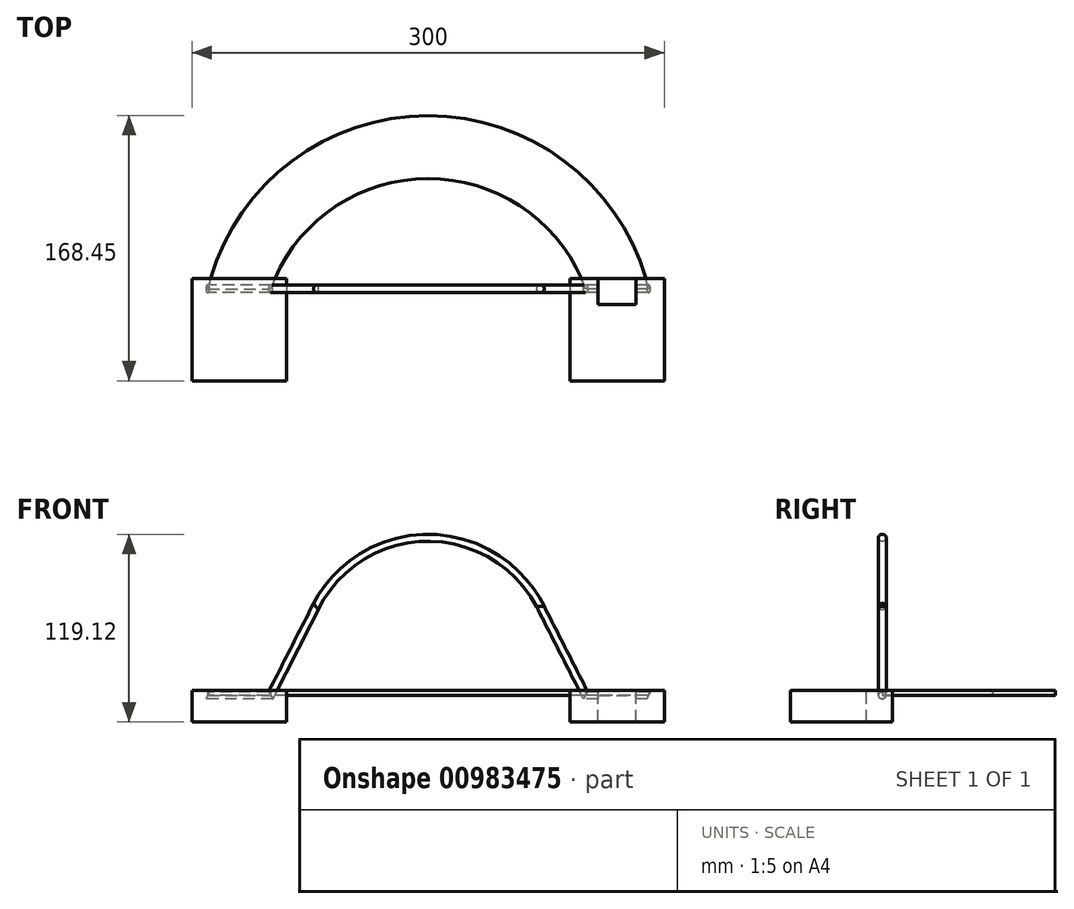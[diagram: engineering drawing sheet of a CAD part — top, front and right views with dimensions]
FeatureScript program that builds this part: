
annotation { "Feature Type Name" : "Feature", "Feature Type Description" : "" }
export const myFeature = defineFeature(function(context is Context, id is Id, definition is map)
    precondition{}
    {
        {
            var Q0;
            Q0=qCreatedBy(makeId("Top.planeOp"),FACE);
            var sketch = newSketch(context, id + "F0", { "sketchPlane" : qUnion([Q0])});
            skLineSegment(sketch, "E0", {"start": v(-140, 0) * mm, "end": v(140, 0) * mm});
            skPoint(sketch, "E1", {"position": v(0, 0) * mm});
            skCircle(sketch, "E2", {"center": v(0, 0) * mm, "radius": 97.97 * mm});
            skSolve(sketch);
        }
        {
            var Q0;
            Q0=qCreatedBy(makeId("Top.planeOp"),FACE);
            var sketch = newSketch(context, id + "F1", { "sketchPlane" : qUnion([Q0])});
            skLineSegment(sketch, "E3", {"start": v(-100, 0) * mm, "end": v(100, 0) * mm});
            skPoint(sketch, "E4", {"position": v(0, 0) * mm});
            skLineSegment(sketch, "E5", {"start": v(0, 0) * mm, "end": v(0, 70) * mm});
            skArc(sketch, "E6", {"start": v(100, 0) * mm, "mid": v(0, 70) * mm, "end": v(-100, 0) * mm});
            skSolve(sketch);
        }
        {
            var Q0;
            Q0=qCreatedBy(makeId("Top.planeOp"),FACE);
            var sketch = newSketch(context, id + "F2", { "sketchPlane" : qUnion([Q0])});
            skPoint(sketch, "E7", {"position": v(0, 0) * mm});
            skLineSegment(sketch, "E8", {"start": v(0, 0) * mm, "end": v(0, 70) * mm});
            skArc(sketch, "E9", {"start": v(100, 0) * mm, "mid": v(0, 70) * mm, "end": v(-100, 0) * mm});
            skArc(sketch, "E10.0", {"start": v(121.07, 0) * mm, "mid": v(0, 90) * mm, "end": v(-121.07, 0) * mm});
            skLineSegment(sketch, "E11", {"start": v(-140, 0) * mm, "end": v(-100, 0) * mm});
            skLineSegment(sketch, "E12", {"start": v(0, 0) * mm, "end": v(0, 110) * mm});
            skLineSegment(sketch, "E13", {"start": v(140, 0) * mm, "end": v(100, 0) * mm});
            skArc(sketch, "E14", {"start": v(140, 0) * mm, "mid": v(0, 110) * mm, "end": v(-140, 0) * mm});
            skLineSegment(sketch, "E15.trimOffspring", {"start": v(100, 0) * mm, "end": v(140, 0) * mm});
            skLineSegment(sketch, "E16.trimOffspring", {"start": v(-100, 0) * mm, "end": v(-140, 0) * mm});
            skSolve(sketch);
        }
        {
            var Q0;
            Q0=qCreatedBy(makeId("Front.planeOp"),FACE);
            var sketch = newSketch(context, id + "F3", { "sketchPlane" : qUnion([Q0])});
            skLineSegment(sketch, "E17", {"start": v(0, 0) * mm, "end": v(0, 20) * mm});
            skPoint(sketch, "E18.0", {"position": v(100, 0) * mm});
            skPoint(sketch, "E19.0", {"position": v(-100, 0) * mm});
            skArc(sketch, "E20", {"start": v(71.27, 56.34) * mm, "mid": v(0, 100) * mm, "end": v(-71.27, 56.34) * mm});
            skLineSegment(sketch, "E21", {"start": v(-100, 0) * mm, "end": v(-71.27, 56.34) * mm});
            skLineSegment(sketch, "E22", {"start": v(100, 0) * mm, "end": v(71.27, 56.34) * mm});
            skSolve(sketch);
        }
        {
            var Q0;
            Q0=qCreatedBy(makeId("Top.planeOp"),FACE);
            var sketch = newSketch(context, id + "F4", { "sketchPlane" : qUnion([Q0])});
            skPoint(sketch, "E23.0", {"position": v(100, 0) * mm});
            skCircle(sketch, "E24", {"center": v(100, 0) * mm, "radius": 2.5 * mm});
            skSolve(sketch);
        }
        {
            var Q0;
            Q0=makeQuery(id+"F4.imprint","IMPRINT",FACE,{"disambiguationData":[TD([[makeQuery(id+"F4.imprint","IMPRINT",EDGE,{"derivedFrom":sQuery(id+"F4.wireOp",EDGE,"E24")}),1.0]])]});
            var Q1;
            Q1=sQuery(id+"F3.wireOp",EDGE,"E22");
            var Q2;
            Q2=sQuery(id+"F3.wireOp",EDGE,"E20");
            var Q3;
            Q3=sQuery(id+"F3.wireOp",EDGE,"E21");
            var Q4;
            Q4=sQuery(id+"F2.wireOp",EDGE,"E11");
            var Q5;
            Q5=sQuery(id+"F2.wireOp",EDGE,"E13");
            sweep(context, id + "F5", {"profiles" : qUnion([Q0]), "path" : qUnion([Q1, Q2, Q3, Q4, Q5])});
        }
        {
            var Q0;
            {var subQ0=sQuery(id+"F2.wireOp",EDGE,"E15.trimOffspring");var subQ1=sQuery(id+"F2.wireOp",EDGE,"E9");var subQ2=makeQuery(id+"F2.imprint","INTERSECT",VERTEX,{"derivedFrom":[subQ1,subQ0]});Q0=makeQuery(id+"F2.imprint","IMPRINT",FACE,{"disambiguationData":[TD([[makeQuery(id+"F2.imprint","IMPRINT",EDGE,{"disambiguationData":[TD([[subQ2,-1.0]])],"derivedFrom":subQ1}),-1.0]])]});}
            var Q1;
            {var subQ0=sQuery(id+"F2.wireOp",EDGE,"E16.trimOffspring");var subQ1=sQuery(id+"F2.wireOp",EDGE,"E9");var subQ2=makeQuery(id+"F2.imprint","INTERSECT",VERTEX,{"derivedFrom":[subQ1,subQ0]});Q1=makeQuery(id+"F2.imprint","IMPRINT",FACE,{"disambiguationData":[TD([[makeQuery(id+"F2.imprint","IMPRINT",EDGE,{"disambiguationData":[TD([[subQ2,1.0]])],"derivedFrom":subQ1}),-1.0]])]});}
            var Q2;
            {var subQ0=sQuery(id+"F2.wireOp",EDGE,"E16.trimOffspring");var subQ1=sQuery(id+"F2.wireOp",EDGE,"E10.0");var subQ2=makeQuery(id+"F2.imprint","INTERSECT",VERTEX,{"derivedFrom":[subQ1,subQ0]});Q2=makeQuery(id+"F2.imprint","IMPRINT",FACE,{"disambiguationData":[TD([[makeQuery(id+"F2.imprint","IMPRINT",EDGE,{"disambiguationData":[TD([[subQ2,1.0]])],"derivedFrom":subQ1}),-1.0]])]});}
            var Q3;
            {var subQ0=sQuery(id+"F2.wireOp",EDGE,"E15.trimOffspring");var subQ1=sQuery(id+"F2.wireOp",EDGE,"E10.0");var subQ2=makeQuery(id+"F2.imprint","INTERSECT",VERTEX,{"derivedFrom":[subQ1,subQ0]});Q3=makeQuery(id+"F2.imprint","IMPRINT",FACE,{"disambiguationData":[TD([[makeQuery(id+"F2.imprint","IMPRINT",EDGE,{"disambiguationData":[TD([[subQ2,-1.0]])],"derivedFrom":subQ1}),-1.0]])]});}
            extrude(context, id + "F6", {"entities" : qUnion([Q0, Q1, Q2, Q3]), "depth" : 3 * mm, "offsetDistance" : 25 * mm});
        }
        {
            var Q0;
            Q0=qCreatedBy(makeId("Right.planeOp"),FACE);
            cPlane(context, id + "F7", {"entities" : qUnion([Q0]), "cplaneType" : CPlaneType.OFFSET, "offset" : 150 * mm, "width" : 150 * mm, "height" : 150 * mm});
        }
        {
            var Q0;
            Q0=qCreatedBy(id+"F7.planeOp",FACE);
            var sketch = newSketch(context, id + "F8", { "sketchPlane" : qUnion([Q0])});
            skLineSegment(sketch, "E25.bottom", {"start": v(6.55, 3.11) * mm, "end": v(-58.45, 3.11) * mm});
            skLineSegment(sketch, "E25.top", {"start": v(6.55, -16.89) * mm, "end": v(-58.45, -16.89) * mm});
            skLineSegment(sketch, "E25.left", {"start": v(6.55, 3.11) * mm, "end": v(6.55, -16.89) * mm});
            skLineSegment(sketch, "E25.right", {"start": v(-58.45, 3.11) * mm, "end": v(-58.45, -16.89) * mm});
            skSolve(sketch);
        }
        {
            var Q0;
            Q0=makeQuery(id+"F8.imprint","IMPRINT",FACE,{"disambiguationData":[TD([[makeQuery(id+"F8.imprint","IMPRINT",EDGE,{"derivedFrom":sQuery(id+"F8.wireOp",EDGE,"E25.bottom")}),1.0]])]});
            extrude(context, id + "F9", {"entities" : qUnion([Q0]), "oppositeDirection" : true, "depth" : 60 * mm, "offsetDistance" : 25 * mm});
        }
        {
            var Q0;
            Q0=makeQuery(id+"F9.opExtrude","SWEPT_BODY",BODY,{"disambiguationData":[OSD([sQuery(id+"F8.wireOp",EDGE,"E25.bottom"),sQuery(id+"F8.wireOp",EDGE,"E25.top"),sQuery(id+"F8.wireOp",EDGE,"E25.left"),sQuery(id+"F8.wireOp",EDGE,"E25.right")])]});
            var Q1;
            Q1=qCreatedBy(makeId("Right.planeOp"),FACE);
            mirror(context, id + "F10", {"entities" : qUnion([Q0]), "mirrorPlane" : qUnion([Q1])});
        }
        {
            var Q0;
            Q0=makeQuery(id+"F9.opExtrude","SWEPT_FACE",FACE,{"disambiguationData":[OSD([sQuery(id+"F8.wireOp",EDGE,"E25.bottom")])]});
            var sketch = newSketch(context, id + "F11", { "sketchPlane" : qUnion([Q0])});
            skArc(sketch, "E26.0", {"start": v(100, 0) * mm, "mid": v(0, 70) * mm, "end": v(-100, 0) * mm});
            skArc(sketch, "E27.0", {"start": v(140, 0) * mm, "mid": v(0, 110) * mm, "end": v(-140, 0) * mm});
            skLineSegment(sketch, "E28.0", {"start": v(90, 6.55) * mm, "end": v(150, 6.55) * mm});
            skLineSegment(sketch, "E29", {"start": v(100, 0) * mm, "end": v(100, -10) * mm});
            skLineSegment(sketch, "E30", {"start": v(140, 0) * mm, "end": v(140, -10) * mm});
            skLineSegment(sketch, "E31.0", {"start": v(132, 0) * mm, "end": v(132, -30) * mm});
            skLineSegment(sketch, "E32.0", {"start": v(108, 0) * mm, "end": v(108, -10) * mm});
            skLineSegment(sketch, "E33.bottom", {"start": v(108, -10) * mm, "end": v(132, -10) * mm});
            skLineSegment(sketch, "E33.top", {"start": v(108, 6.55) * mm, "end": v(132, 6.55) * mm});
            skLineSegment(sketch, "E33.left", {"start": v(108, -10) * mm, "end": v(108, 6.55) * mm});
            skLineSegment(sketch, "E33.right", {"start": v(132, -10) * mm, "end": v(132, 6.55) * mm});
            skSolve(sketch);
        }
        {
            var Q0;
            Q0 = qSketchRegion(id + "F11", true);
            extrude(context, id + "F12", {"entities" : qUnion([Q0]), "operationType" : NewBodyOperationType.REMOVE, "oppositeDirection" : true, "depth" : 25 * mm, "offsetDistance" : 25 * mm});
        }
    });
